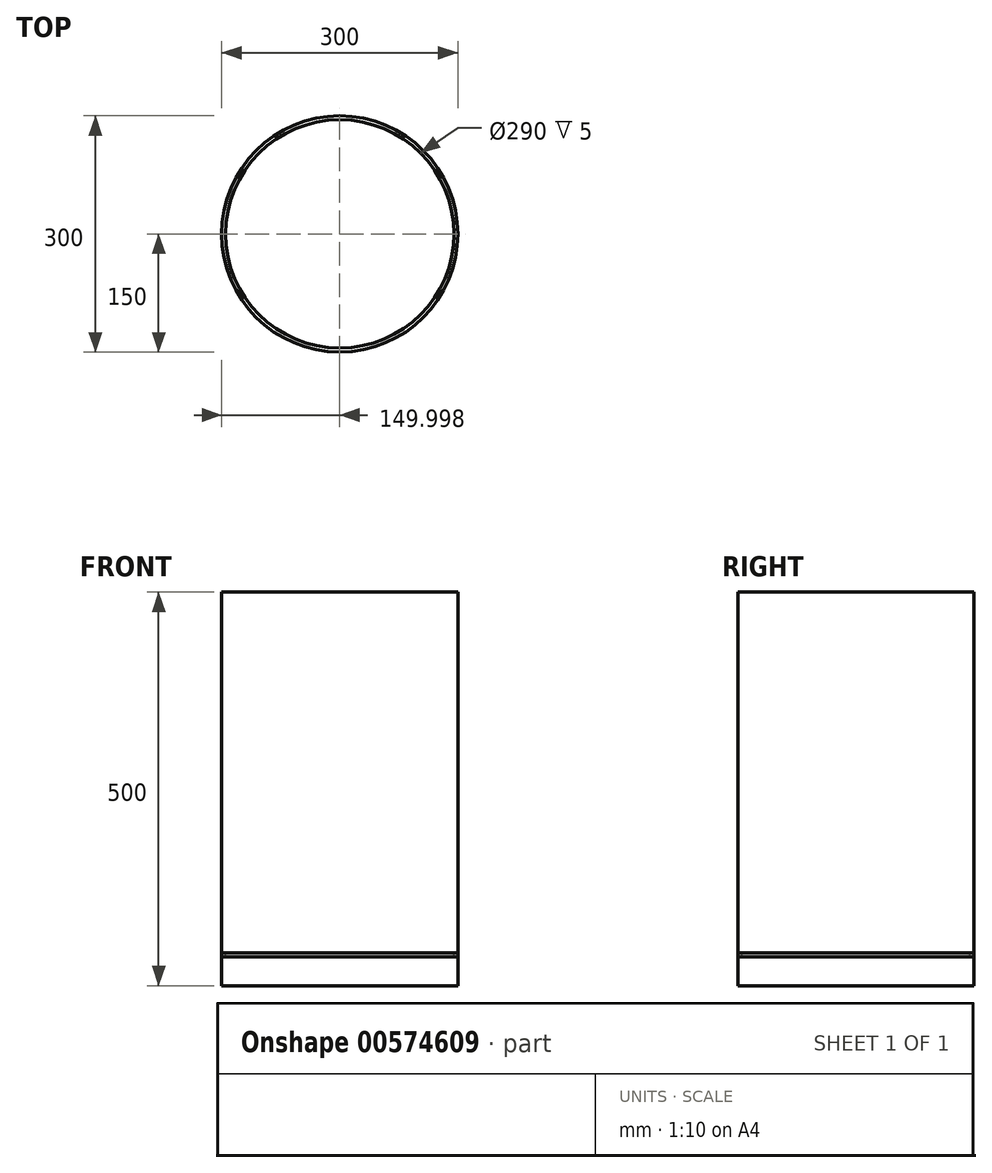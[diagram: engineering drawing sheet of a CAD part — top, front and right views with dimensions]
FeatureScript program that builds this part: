
annotation { "Feature Type Name" : "Feature", "Feature Type Description" : "" }
export const myFeature = defineFeature(function(context is Context, id is Id, definition is map)
    precondition{}
    {
        {
            var Q0;
            Q0=qCreatedBy(makeId("Front.planeOp"),FACE);
            var sketch = newSketch(context, id + "F0", { "sketchPlane" : qUnion([Q0])});
            skLineSegment(sketch, "E0", {"start": v(-150.08, 499.88) * mm, "end": v(-150.08, -0.12) * mm});
            skLineSegment(sketch, "E1", {"start": v(-150.08, -0.12) * mm, "end": v(149.92, -0.12) * mm});
            skLineSegment(sketch, "E2.0", {"start": v(149.92, 499.88) * mm, "end": v(149.92, -0.12) * mm});
            skLineSegment(sketch, "E3.0", {"start": v(-0.08, -0.12) * mm, "end": v(-0.08, 38.34) * mm});
            skLineSegment(sketch, "E4.bottom", {"start": v(-150.08, 41.72) * mm, "end": v(-145.08, 41.72) * mm});
            skLineSegment(sketch, "E4.top", {"start": v(-150.08, 36.72) * mm, "end": v(-145.08, 36.72) * mm});
            skLineSegment(sketch, "E4.left", {"start": v(-150.08, 41.72) * mm, "end": v(-150.08, 36.72) * mm});
            skLineSegment(sketch, "E4.right", {"start": v(-145.08, 41.72) * mm, "end": v(-145.08, 36.72) * mm});
            skSolve(sketch);
        }
        {
            var Q0;
            Q0=sQuery(id+"F0.wireOp",EDGE,"E0");
            var Q1;
            Q1=sQuery(id+"F0.wireOp",EDGE,"E3.0");
            revolve(context, id + "F1", {"bodyType" : ToolBodyType.SURFACE, "surfaceEntities" : qUnion([Q0]), "axis" : qUnion([Q1]), "revolveType" : RevolveType.FULL});
        }
        {
            var Q0;
            Q0 = qSketchRegion(id + "F0", true);
            var Q1;
            Q1=sQuery(id+"F0.wireOp",EDGE,"E4.left");
            var Q2;
            Q2=sQuery(id+"F0.wireOp",EDGE,"E4.bottom");
            var Q3;
            Q3=sQuery(id+"F0.wireOp",EDGE,"E4.right");
            var Q4;
            Q4=sQuery(id+"F0.wireOp",EDGE,"E4.top");
            var Q5;
            Q5=sQuery(id+"F0.wireOp",EDGE,"E3.0");
            revolve(context, id + "F2", {"bodyType" : ToolBodyType.SURFACE, "entities" : qUnion([Q0]), "surfaceEntities" : qUnion([Q1, Q2, Q3, Q4]), "axis" : qUnion([Q5]), "revolveType" : RevolveType.FULL});
        }
    });
